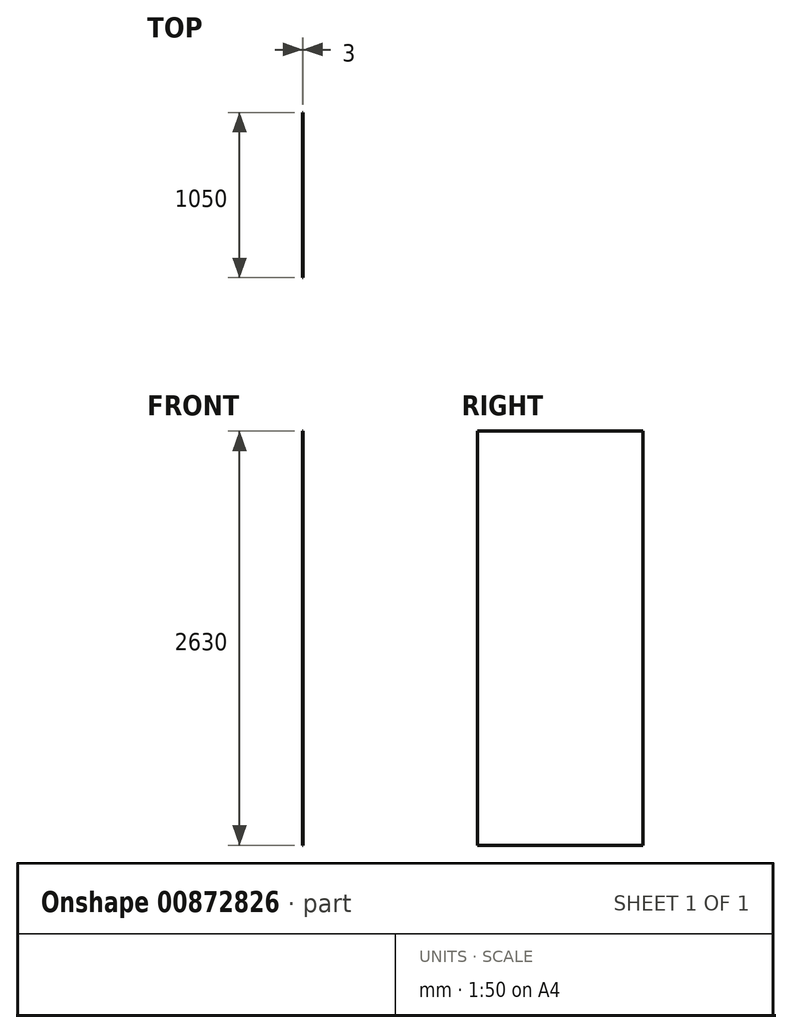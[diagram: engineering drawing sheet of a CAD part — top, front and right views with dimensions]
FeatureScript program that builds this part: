
annotation { "Feature Type Name" : "Feature", "Feature Type Description" : "" }
export const myFeature = defineFeature(function(context is Context, id is Id, definition is map)
    precondition{}
    {
        {
            var Q0;
            Q0=qCreatedBy(makeId("Right.planeOp"),FACE);
            var sketch = newSketch(context, id + "F0", { "sketchPlane" : qUnion([Q0])});
            skLineSegment(sketch, "E0.bottom", {"start": v(-478.68, 1315) * mm, "end": v(571.32, 1315) * mm});
            skLineSegment(sketch, "E0.top", {"start": v(-478.68, -1315) * mm, "end": v(571.32, -1315) * mm});
            skLineSegment(sketch, "E0.left", {"start": v(-478.68, 1315) * mm, "end": v(-478.68, -1315) * mm});
            skLineSegment(sketch, "E0.right", {"start": v(571.32, 1315) * mm, "end": v(571.32, -1315) * mm});
            skPoint(sketch, "E0.middle", {"position": v(46.32, 0) * mm});
            skSolve(sketch);
        }
        {
            var Q0;
            Q0 = qSketchRegion(id + "F0", true);
            extrude(context, id + "F1", {"entities" : qUnion([Q0]), "depth" : 3 * mm, "offsetDistance" : 25 * mm});
        }
    });
